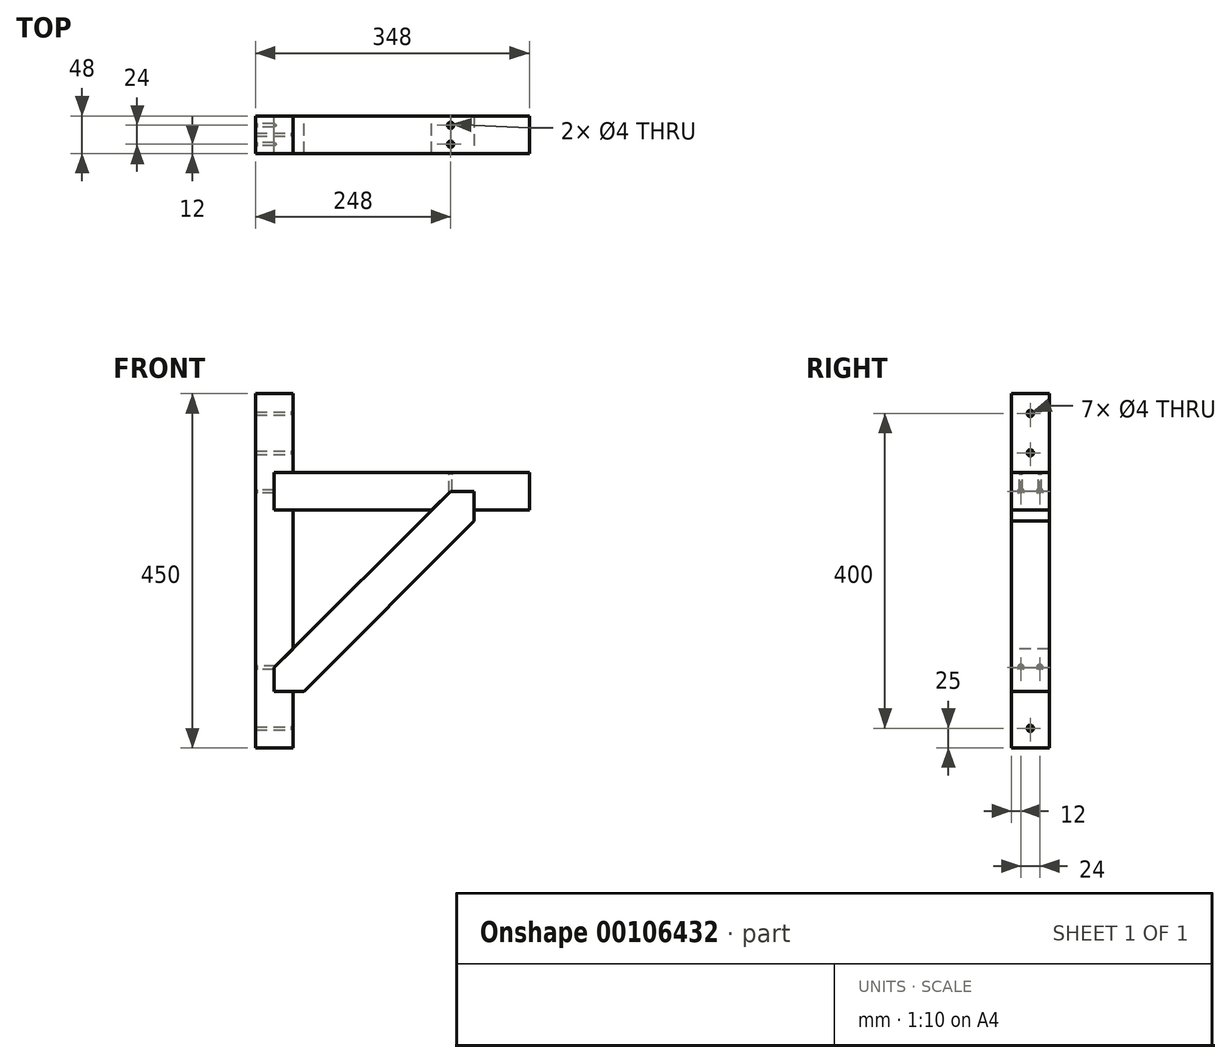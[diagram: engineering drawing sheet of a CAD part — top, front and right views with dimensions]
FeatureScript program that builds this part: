
annotation { "Feature Type Name" : "Feature", "Feature Type Description" : "" }
export const myFeature = defineFeature(function(context is Context, id is Id, definition is map)
    precondition{}
    {
        {
            var Q0;
            Q0=qCreatedBy(makeId("Top.planeOp"),FACE);
            var sketch = newSketch(context, id + "F0", { "sketchPlane" : qUnion([Q0])});
            skLineSegment(sketch, "E0.bottom", {"start": v(24, -24) * mm, "end": v(-24, -24) * mm});
            skLineSegment(sketch, "E0.top", {"start": v(24, 24) * mm, "end": v(-24, 24) * mm});
            skLineSegment(sketch, "E0.left", {"start": v(24, -24) * mm, "end": v(24, 24) * mm});
            skLineSegment(sketch, "E0.right", {"start": v(-24, -24) * mm, "end": v(-24, 24) * mm});
            skPoint(sketch, "E0.middle", {"position": v(0, 0) * mm});
            skSolve(sketch);
        }
        {
            var Q0;
            Q0=makeQuery(id+"F0.imprint","IMPRINT",FACE,{"disambiguationData":[TD([[makeQuery(id+"F0.imprint","IMPRINT",EDGE,{"derivedFrom":sQuery(id+"F0.wireOp",EDGE,"E0.bottom")}),-1.0]])]});
            extrude(context, id + "F1", {"entities" : qUnion([Q0]), "depth" : 400 * mm, "hasSecondDirection" : true, "secondDirectionOppositeDirection" : true, "secondDirectionDepth" : 50 * mm});
        }
        {
            var Q0;
            Q0=qCreatedBy(makeId("Front.planeOp"),FACE);
            var sketch = newSketch(context, id + "F2", { "sketchPlane" : qUnion([Q0])});
            skLineSegment(sketch, "E1.bottom", {"start": v(324, 300) * mm, "end": v(0, 300) * mm});
            skLineSegment(sketch, "E1.top", {"start": v(324, 252) * mm, "end": v(0, 252) * mm});
            skLineSegment(sketch, "E1.left", {"start": v(324, 300) * mm, "end": v(324, 252) * mm});
            skLineSegment(sketch, "E1.right", {"start": v(0, 300) * mm, "end": v(0, 252) * mm});
            skSolve(sketch);
        }
        {
            var Q0;
            Q0=makeQuery(id+"F2.imprint","IMPRINT",FACE,{"disambiguationData":[TD([[makeQuery(id+"F2.imprint","IMPRINT",EDGE,{"derivedFrom":sQuery(id+"F2.wireOp",EDGE,"E1.bottom")}),1.0]])]});
            extrude(context, id + "F3", {"entities" : qUnion([Q0]), "operationType" : NewBodyOperationType.REMOVE, "endBound" : BoundingType.SYMMETRIC, "depth" : 48 * mm});
        }
        {
            var Q0;
            Q0=qCreatedBy(makeId("Front.planeOp"),FACE);
            var sketch = newSketch(context, id + "F4", { "sketchPlane" : qUnion([Q0])});
            skLineSegment(sketch, "E2", {"start": v(224, 276) * mm, "end": v(0, 52) * mm});
            skLineSegment(sketch, "E3", {"start": v(0, 52) * mm, "end": v(0, 22) * mm});
            skLineSegment(sketch, "E4", {"start": v(37.88, 22) * mm, "end": v(254, 238.12) * mm});
            skLineSegment(sketch, "E5", {"start": v(254, 276) * mm, "end": v(224, 276) * mm});
            skLineSegment(sketch, "E6", {"start": v(254, 238.12) * mm, "end": v(254, 276) * mm});
            skLineSegment(sketch, "E7", {"start": v(0, 22) * mm, "end": v(37.88, 22) * mm});
            skSolve(sketch);
        }
        {
            var Q0;
            Q0=makeQuery(id+"F4.imprint","IMPRINT",FACE,{"disambiguationData":[TD([[makeQuery(id+"F4.imprint","IMPRINT",EDGE,{"derivedFrom":sQuery(id+"F4.wireOp",EDGE,"E2")}),1.0]])]});
            extrude(context, id + "F5", {"entities" : qUnion([Q0]), "operationType" : NewBodyOperationType.REMOVE, "endBound" : BoundingType.SYMMETRIC, "depth" : 48 * mm});
        }
        {
            var Q0;
            Q0 = qSketchRegion(id + "F2", true);
            extrude(context, id + "F6", {"entities" : qUnion([Q0]), "endBound" : BoundingType.SYMMETRIC, "depth" : 48 * mm});
        }
        {
            var Q0;
            Q0 = qSketchRegion(id + "F4", true);
            extrude(context, id + "F7", {"entities" : qUnion([Q0]), "operationType" : NewBodyOperationType.REMOVE, "endBound" : BoundingType.SYMMETRIC, "oppositeDirection" : true, "depth" : 48 * mm});
        }
        {
            var Q0;
            Q0 = qSketchRegion(id + "F4", true);
            extrude(context, id + "F8", {"entities" : qUnion([Q0]), "endBound" : BoundingType.SYMMETRIC, "depth" : 48 * mm});
        }
        {
            var Q0;
            Q0 = qSketchRegion(id + "F4", true);
            extrude(context, id + "F9", {"entities" : qUnion([Q0]), "depth" : 25 * mm});
        }
        {
            var Q0;
            Q0=makeQuery(id+"F9.opExtrude","SWEPT_BODY",BODY,{"disambiguationData":[OSD([sQuery(id+"F4.wireOp",EDGE,"E2"),sQuery(id+"F4.wireOp",EDGE,"E3"),sQuery(id+"F4.wireOp",EDGE,"E4"),sQuery(id+"F4.wireOp",EDGE,"E5"),sQuery(id+"F4.wireOp",EDGE,"E6"),sQuery(id+"F4.wireOp",EDGE,"E7")])]});
            deleteBodies(context, id + "F10", {"entities" : qUnion([Q0])});
        }
        {
            var Q0;
            Q0=makeQuery(id+"F6.opExtrude","SWEPT_FACE",FACE,{"disambiguationData":[OSD([sQuery(id+"F2.wireOp",EDGE,"E1.bottom")])]});
            var sketch = newSketch(context, id + "F11", { "sketchPlane" : qUnion([Q0])});
            skPoint(sketch, "E8", {"position": v(224, 12) * mm});
            skPoint(sketch, "E9.MirrorP", {"position": v(224, -12) * mm});
            skSolve(sketch);
        }
        {
            var Q0;
            Q0=sQuery(id+"F11.wireOp",VERTEX,"E9.MirrorP");
            var Q1;
            Q1=sQuery(id+"F11.wireOp",VERTEX,"E8");
            var Q2;
            Q2=makeQuery(id+"F6.opExtrude","SWEPT_BODY",BODY,{"disambiguationData":[OSD([sQuery(id+"F2.wireOp",EDGE,"E1.bottom"),sQuery(id+"F2.wireOp",EDGE,"E1.top"),sQuery(id+"F2.wireOp",EDGE,"E1.left"),sQuery(id+"F2.wireOp",EDGE,"E1.right")])]});
            hole(context, id + "F12", {"style" : HoleStyle.C_SINK, "endStyle" : HoleEndStyle.THROUGH, "holeDiameter" : 4 * mm, "cSinkDiameter" : 8 * mm, "cSinkAngle" : 90 * degree, "startFromSketch" : true, "locations" : qUnion([Q0, Q1]), "scope" : qUnion([Q2]), "isTappedThrough" : true});
        }
        {
            var Q0;
            Q0=makeQuery(id+"F1.opExtrude","SWEPT_FACE",FACE,{"disambiguationData":[OSD([sQuery(id+"F0.wireOp",EDGE,"E0.right")])]});
            var sketch = newSketch(context, id + "F13", { "sketchPlane" : qUnion([Q0])});
            skPoint(sketch, "E10", {"position": v(12, 52) * mm});
            skPoint(sketch, "E11", {"position": v(12, 276) * mm});
            skPoint(sketch, "E12.MirrorP", {"position": v(-12, 276) * mm});
            skPoint(sketch, "E13.MirrorP", {"position": v(-12, 52) * mm});
            skSolve(sketch);
        }
        {
            var Q0;
            Q0=sQuery(id+"F13.wireOp",VERTEX,"E12.MirrorP");
            var Q1;
            Q1=sQuery(id+"F13.wireOp",VERTEX,"E11");
            var Q2;
            Q2=sQuery(id+"F13.wireOp",VERTEX,"E13.MirrorP");
            var Q3;
            Q3=sQuery(id+"F13.wireOp",VERTEX,"E10");
            var Q4;
            Q4=makeQuery(id+"F1.opExtrude","SWEPT_BODY",BODY,{"disambiguationData":[OSD([sQuery(id+"F0.wireOp",EDGE,"E0.bottom"),sQuery(id+"F0.wireOp",EDGE,"E0.top"),sQuery(id+"F0.wireOp",EDGE,"E0.left"),sQuery(id+"F0.wireOp",EDGE,"E0.right")])]});
            hole(context, id + "F14", {"style" : HoleStyle.C_SINK, "endStyle" : HoleEndStyle.THROUGH, "holeDiameter" : 4 * mm, "cSinkDiameter" : 8 * mm, "cSinkAngle" : 90 * degree, "startFromSketch" : true, "locations" : qUnion([Q0, Q1, Q2, Q3]), "scope" : qUnion([Q4]), "isTappedThrough" : true});
        }
        {
            var Q0;
            {var subQ2=sQuery(id+"F0.wireOp",EDGE,"E0.left");Q0=makeQuery(id+"F5.boolean.opBoolean","SPLIT",FACE,{"disambiguationData":[TD([makeQuery(id+"F5.opExtrude","SWEPT_FACE",FACE,{"disambiguationData":[OSD([sQuery(id+"F4.wireOp",EDGE,"E7")])]})])],"derivedFrom":makeQuery(id+"F3.boolean.opBoolean","SPLIT",FACE,{"disambiguationData":[TD([makeQuery(id+"F3.opExtrude","SWEPT_FACE",FACE,{"disambiguationData":[OSD([sQuery(id+"F2.wireOp",EDGE,"E1.top")])]})])],"derivedFrom":makeQuery(id+"F1.opExtrude","SWEPT_FACE",FACE,{"disambiguationData":[OSD([subQ2])]})})});}
            var sketch = newSketch(context, id + "F15", { "sketchPlane" : qUnion([Q0])});
            skPoint(sketch, "E14", {"position": v(0, -25) * mm});
            skPoint(sketch, "E15", {"position": v(0, 375) * mm});
            skPoint(sketch, "E16", {"position": v(0, 325) * mm});
            skSolve(sketch);
        }
        {
            var Q0;
            Q0=sQuery(id+"F15.wireOp",VERTEX,"E15");
            var Q1;
            Q1=sQuery(id+"F15.wireOp",VERTEX,"E16");
            var Q2;
            Q2=sQuery(id+"F15.wireOp",VERTEX,"E14");
            var Q3;
            Q3=makeQuery(id+"F1.opExtrude","SWEPT_BODY",BODY,{"disambiguationData":[OSD([sQuery(id+"F0.wireOp",EDGE,"E0.bottom"),sQuery(id+"F0.wireOp",EDGE,"E0.top"),sQuery(id+"F0.wireOp",EDGE,"E0.left"),sQuery(id+"F0.wireOp",EDGE,"E0.right")])]});
            hole(context, id + "F16", {"style" : HoleStyle.C_SINK, "endStyle" : HoleEndStyle.THROUGH, "holeDiameter" : 4 * mm, "cSinkDiameter" : 8 * mm, "cSinkAngle" : 90 * degree, "startFromSketch" : true, "locations" : qUnion([Q0, Q1, Q2]), "scope" : qUnion([Q3]), "isTappedThrough" : true});
        }
    });
